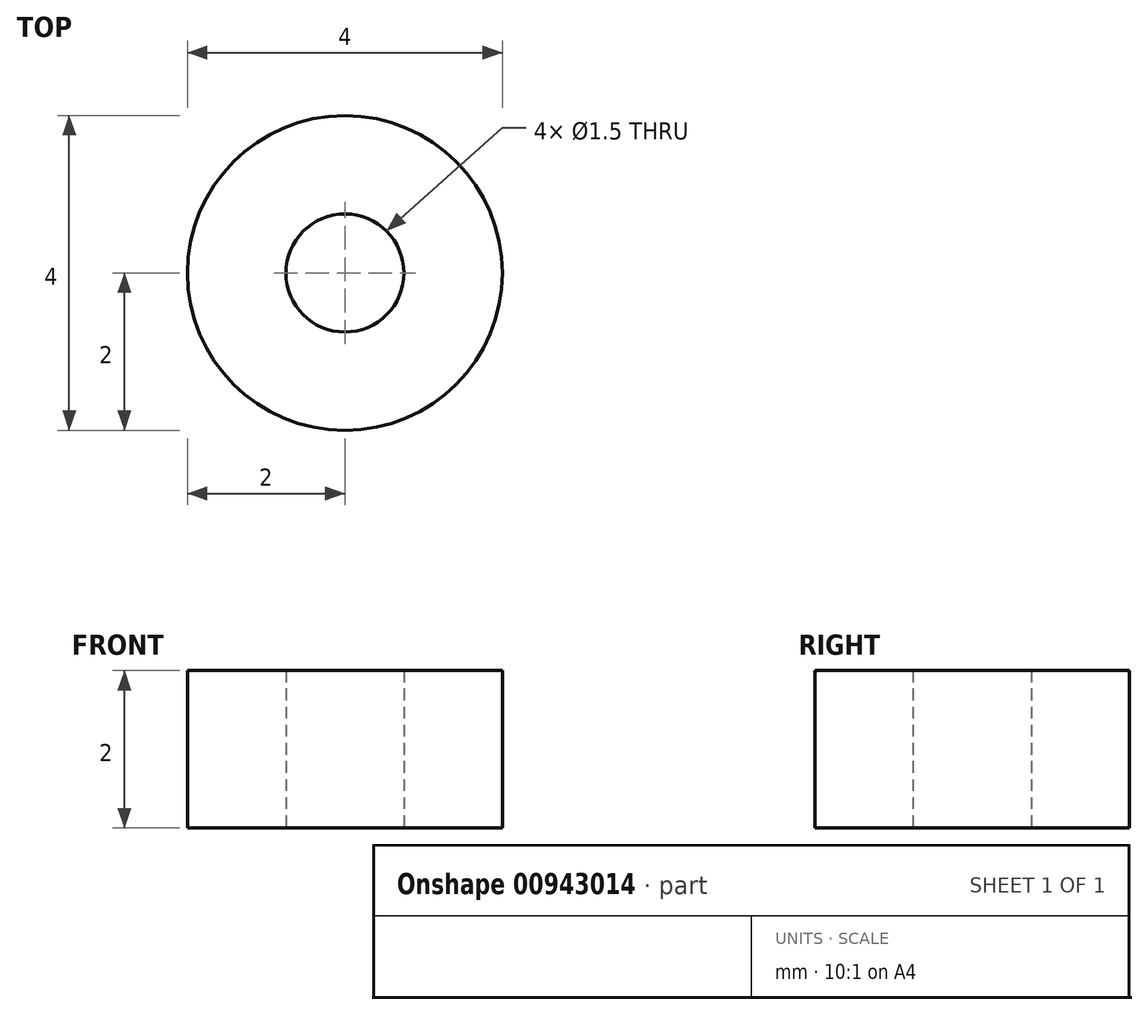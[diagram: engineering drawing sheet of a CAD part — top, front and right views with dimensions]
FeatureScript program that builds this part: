
annotation { "Feature Type Name" : "Feature", "Feature Type Description" : "" }
export const myFeature = defineFeature(function(context is Context, id is Id, definition is map)
    precondition{}
    {
        {
            var Q0;
            Q0=qCreatedBy(makeId("Top.planeOp"),FACE);
            var sketch = newSketch(context, id + "F0", { "sketchPlane" : qUnion([Q0])});
            skCircle(sketch, "E0", {"center": v(0, 0) * mm, "radius": 0.75 * mm});
            skCircle(sketch, "E1", {"center": v(0, 0) * mm, "radius": 2 * mm});
            skSolve(sketch);
        }
        {
            var Q0;
            Q0 = qSketchRegion(id + "F0", true);
            extrude(context, id + "F1", {"entities" : qUnion([Q0]), "depth" : 2 * mm, "offsetDistance" : 25 * mm});
        }
    });
